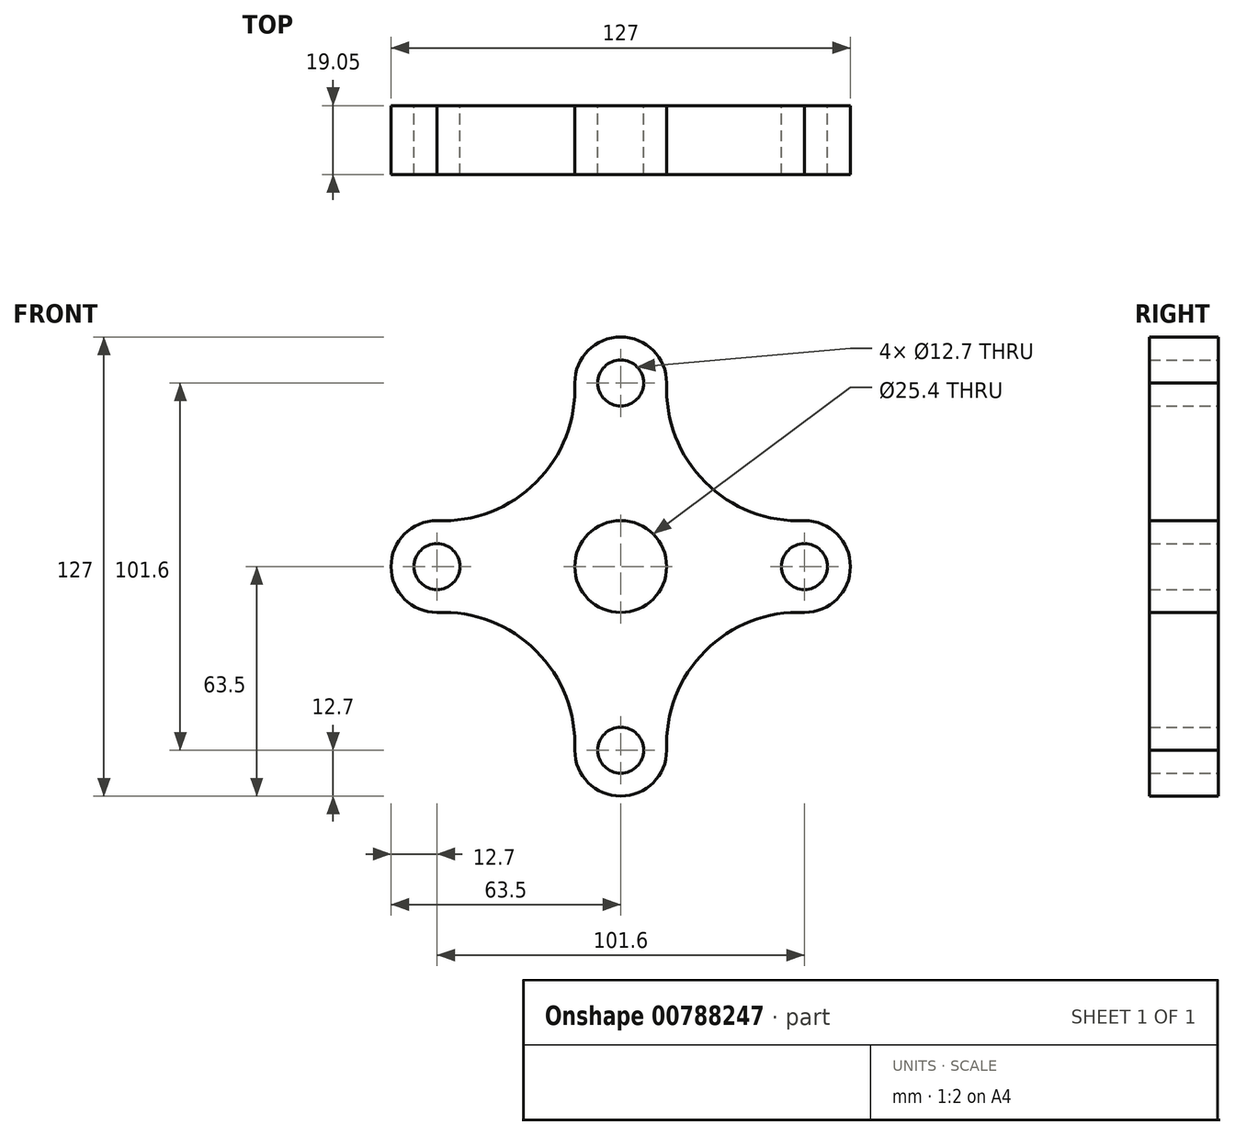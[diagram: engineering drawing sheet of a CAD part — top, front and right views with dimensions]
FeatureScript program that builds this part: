
annotation { "Feature Type Name" : "Feature", "Feature Type Description" : "" }
export const myFeature = defineFeature(function(context is Context, id is Id, definition is map)
    precondition{}
    {
        {
            var Q0;
            Q0=qCreatedBy(makeId("Front.planeOp"),FACE);
            var sketch = newSketch(context, id + "F0", { "sketchPlane" : qUnion([Q0])});
            skLineSegment(sketch, "E0", {"start": v(0, -12.7) * mm, "end": v(0, -50.8) * mm});
            skCircle(sketch, "E1", {"center": v(0, 0) * mm, "radius": 12.7 * mm});
            skLineSegment(sketch, "E2", {"start": v(-12.7, 0) * mm, "end": v(-44.45, 0) * mm});
            skCircle(sketch, "E3", {"center": v(-50.8, 0) * mm, "radius": 6.35 * mm});
            skCircle(sketch, "E4", {"center": v(50.8, 0) * mm, "radius": 6.35 * mm});
            skCircle(sketch, "E5", {"center": v(0, -50.8) * mm, "radius": 6.35 * mm});
            skCircle(sketch, "E6", {"center": v(0, 50.8) * mm, "radius": 6.35 * mm});
            skArc(sketch, "E7", {"start": v(-50.8, 12.7) * mm, "mid": v(-63.5, 0) * mm, "end": v(-50.8, -12.7) * mm});
            skArc(sketch, "E8", {"start": v(12.7, 50.8) * mm, "mid": v(0, 63.5) * mm, "end": v(-12.7, 50.8) * mm});
            skArc(sketch, "E9", {"start": v(50.8, -12.7) * mm, "mid": v(63.5, 0) * mm, "end": v(50.8, 12.7) * mm});
            skArc(sketch, "E10", {"start": v(-12.7, -50.8) * mm, "mid": v(0, -63.5) * mm, "end": v(12.7, -50.8) * mm});
            skArc(sketch, "E11", {"start": v(-50.8, 12.7) * mm, "mid": v(-23.36, 23.36) * mm, "end": v(-12.7, 50.8) * mm});
            skArc(sketch, "E12", {"start": v(12.7, 50.8) * mm, "mid": v(23.36, 23.36) * mm, "end": v(50.8, 12.7) * mm});
            skArc(sketch, "E13", {"start": v(50.8, -12.7) * mm, "mid": v(23.36, -23.36) * mm, "end": v(12.7, -50.8) * mm});
            skArc(sketch, "E14", {"start": v(-12.7, -50.8) * mm, "mid": v(-23.36, -23.36) * mm, "end": v(-50.8, -12.7) * mm});
            skSolve(sketch);
        }
        {
            var Q0;
            Q0=qSketchRegion(id+"F0",true);
            extrude(context, id + "F1", {"entities" : qUnion([Q0]), "depth" : 19.05 * mm, "offsetDistance" : 25.4 * mm});
        }
    });
